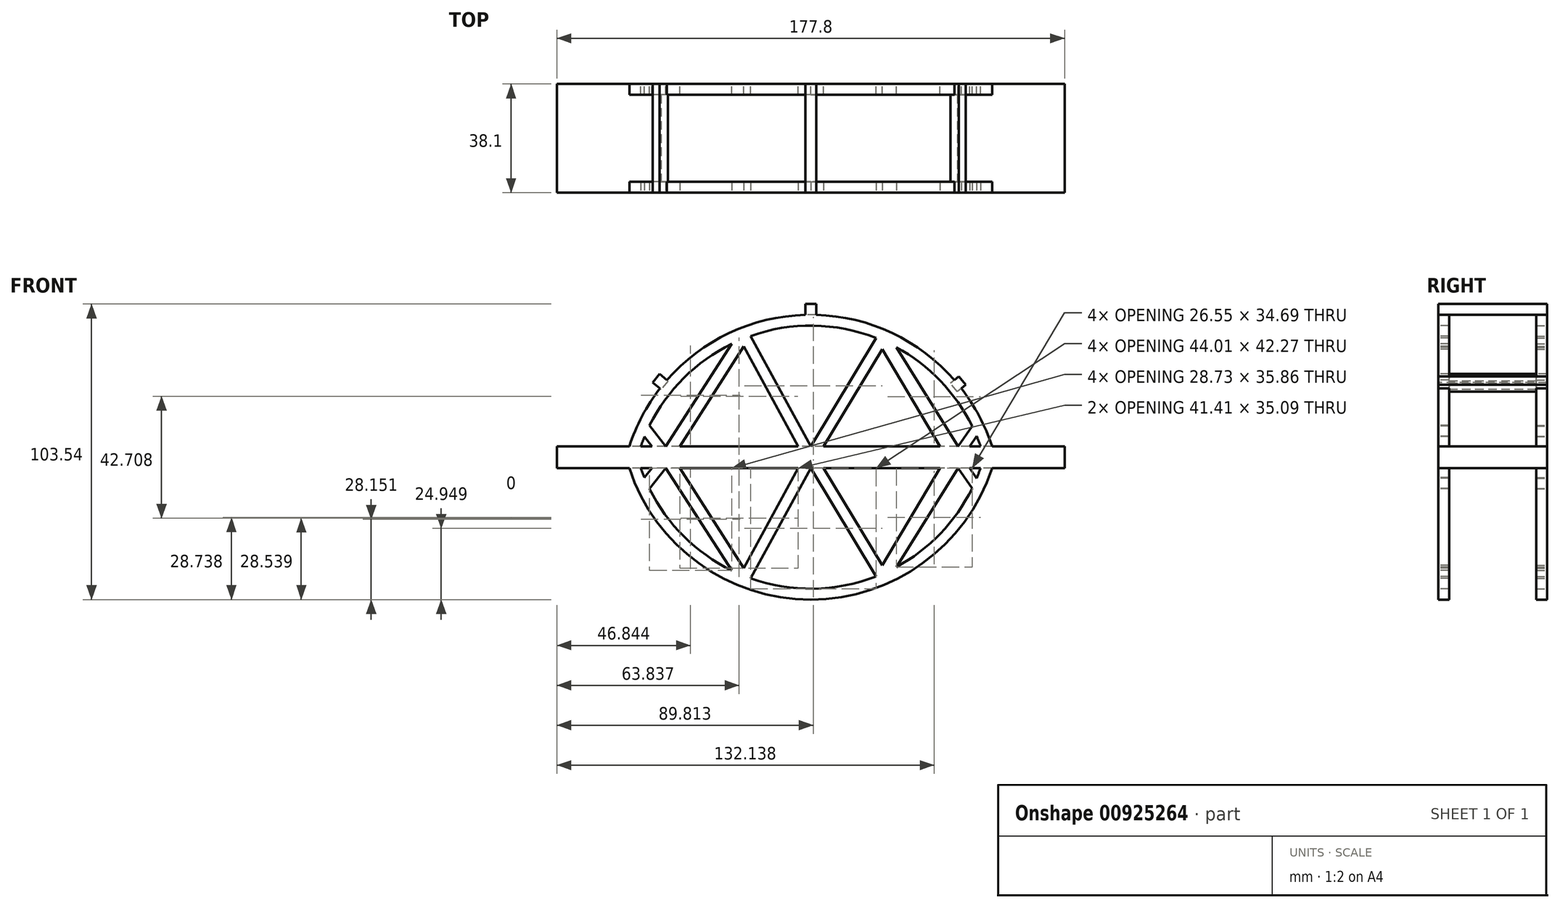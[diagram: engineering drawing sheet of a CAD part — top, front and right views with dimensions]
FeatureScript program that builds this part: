
annotation { "Feature Type Name" : "Feature", "Feature Type Description" : "" }
export const myFeature = defineFeature(function(context is Context, id is Id, definition is map)
    precondition{}
    {
        {
            var Q0;
            Q0=qCreatedBy(makeId("Front.planeOp"),FACE);
            var sketch = newSketch(context, id + "F0", { "sketchPlane" : qUnion([Q0])});
            skLineSegment(sketch, "E0.top", {"start": v(-44.28, -25.57) * mm, "end": v(-11.66, -25.57) * mm});
            skLineSegment(sketch, "E0.left", {"start": v(-47, -21.76) * mm, "end": v(-47, -25.57) * mm});
            skLineSegment(sketch, "E0.right", {"start": v(80, -21.76) * mm, "end": v(80, -25.57) * mm});
            skLineSegment(sketch, "E1", {"start": v(75.99, -21.76) * mm, "end": v(72.12, -21.76) * mm});
            skArc(sketch, "E2", {"start": v(80, -21.76) * mm, "mid": v(16.5, 24.33) * mm, "end": v(-47, -21.76) * mm});
            skLineSegment(sketch, "E3", {"start": v(16.5, -21.76) * mm, "end": v(-4.58, 16.88) * mm});
            skLineSegment(sketch, "E4", {"start": v(-11.18, 14.1) * mm, "end": v(-34.3, -21.76) * mm});
            skLineSegment(sketch, "E5", {"start": v(-34.3, -21.76) * mm, "end": v(-39.91, -14.48) * mm});
            skLineSegment(sketch, "E6", {"start": v(16.5, -21.76) * mm, "end": v(39.43, 16.2) * mm});
            skLineSegment(sketch, "E7", {"start": v(46.47, 12.93) * mm, "end": v(68.06, -21.76) * mm});
            skLineSegment(sketch, "E8", {"start": v(68.06, -21.76) * mm, "end": v(73.03, -14.67) * mm});
            skLineSegment(sketch, "E9.0", {"start": v(12.15, -21.76) * mm, "end": v(-7, 13.33) * mm});
            skLineSegment(sketch, "E10.0", {"start": v(21, -21.76) * mm, "end": v(41.54, 12.26) * mm});
            skLineSegment(sketch, "E11.0", {"start": v(72.12, -21.76) * mm, "end": v(74.62, -18.19) * mm});
            skLineSegment(sketch, "E12.trimOffspring", {"start": v(-39.1, -21.76) * mm, "end": v(-41.7, -18.4) * mm});
            skLineSegment(sketch, "E13.trimOffspring", {"start": v(-7, 13.33) * mm, "end": v(-29.26, -21.76) * mm});
            skLineSegment(sketch, "E14.trimOffspring", {"start": v(12.15, -21.76) * mm, "end": v(-29.26, -21.76) * mm});
            skLineSegment(sketch, "E15.trimOffspring", {"start": v(-39.1, -21.76) * mm, "end": v(-42.97, -21.76) * mm});
            skLineSegment(sketch, "E16.trimOffspring", {"start": v(41.54, 12.26) * mm, "end": v(61.77, -21.76) * mm});
            skLineSegment(sketch, "E17.trimOffspring", {"start": v(61.77, -21.76) * mm, "end": v(21, -21.76) * mm});
            skArc(sketch, "E18.0", {"start": v(75.99, -21.76) * mm, "mid": v(75.33, -19.96) * mm, "end": v(74.62, -18.19) * mm});
            skPoint(sketch, "E19.trimOffspring.end.orphan", {"position": v(-8.9, -21.76) * mm});
            skPoint(sketch, "E20.orphan", {"position": v(-42.49, -11.14) * mm});
            skArc(sketch, "E21.trimOffspring", {"start": v(-41.7, -18.4) * mm, "mid": v(-42.36, -20.07) * mm, "end": v(-42.97, -21.76) * mm});
            skArc(sketch, "E22.trimOffspring", {"start": v(-11.18, 14.1) * mm, "mid": v(-27.9, 2.19) * mm, "end": v(-39.91, -14.48) * mm});
            skArc(sketch, "E23.trimOffspring", {"start": v(39.43, 16.2) * mm, "mid": v(17.49, 20.5) * mm, "end": v(-4.58, 16.88) * mm});
            skArc(sketch, "E24.trimOffspring", {"start": v(39.12, 16.32) * mm, "mid": v(17.2, 20.51) * mm, "end": v(-4.8, 16.8) * mm});
            skPoint(sketch, "E25.orphan", {"position": v(75.5, -11.14) * mm});
            skArc(sketch, "E26.trimOffspring", {"start": v(73.03, -14.67) * mm, "mid": v(61.9, 1.2) * mm, "end": v(46.47, 12.93) * mm});
            skArc(sketch, "E27.trimOffspring", {"start": v(39.43, 16.2) * mm, "mid": v(17.37, 20.51) * mm, "end": v(-4.8, 16.8) * mm});
            skPoint(sketch, "E28.trimOffspring.end.orphan", {"position": v(41.9, -21.76) * mm});
            skPoint(sketch, "E29.start.orphan", {"position": v(16.5, 50.63) * mm});
            skPoint(sketch, "E30.orphan", {"position": v(-47, 50.63) * mm});
            skPoint(sketch, "E31.orphan", {"position": v(80, 50.63) * mm});
            skLineSegment(sketch, "E32", {"start": v(80, -21.76) * mm, "end": v(-47, -21.76) * mm});
            skPoint(sketch, "E33", {"position": v(16.5, 24.33) * mm});
            skPoint(sketch, "E34", {"position": v(68.06, 0) * mm});
            skPoint(sketch, "E35.positionSnap0", {"position": v(61.9, 1.2) * mm});
            skLineSegment(sketch, "E36.trimOffspring", {"start": v(-6.01, -25.57) * mm, "end": v(12.98, -25.57) * mm});
            skLineSegment(sketch, "E37.trimOffspring", {"start": v(19.96, -25.57) * mm, "end": v(39.03, -25.57) * mm});
            skLineSegment(sketch, "E38.trimOffspring", {"start": v(44.66, -25.57) * mm, "end": v(77.29, -25.57) * mm});
            skLineSegment(sketch, "E39", {"start": v(80, -25.57) * mm, "end": v(-47, -25.57) * mm});
            skLineSegment(sketch, "E40", {"start": v(41.69, -25.98) * mm, "end": v(42.08, -25.98) * mm});
            skPoint(sketch, "E41.orphan", {"position": v(41.9, -25.57) * mm});
            skLineSegment(sketch, "E42", {"start": v(16.03, -26.06) * mm, "end": v(16.96, -26.06) * mm});
            skPoint(sketch, "E43.orphan", {"position": v(16.5, -25.57) * mm});
            skLineSegment(sketch, "E44", {"start": v(-9.09, -26.03) * mm, "end": v(-8.52, -26.27) * mm});
            skPoint(sketch, "E45.orphan", {"position": v(-8.9, -25.57) * mm});
            skPoint(sketch, "E46", {"position": v(41.54, 19.46) * mm});
            skPoint(sketch, "E47", {"position": v(-7.55, 19.85) * mm});
            skPoint(sketch, "E48", {"position": v(-35.05, 0) * mm});
            skSolve(sketch);
        }
        {
            var Q0;
            {var subQ7=sQuery(id+"F0.wireOp",EDGE,"E0.left");Q0=makeQuery(id+"F0.imprint","IMPRINT",FACE,{"disambiguationData":[TD([[makeQuery(id+"F0.imprint","IMPRINT",EDGE,{"derivedFrom":subQ7}),1.0]])]});}
            extrude(context, id + "F1", {"entities" : qUnion([Q0]), "depth" : 19.05 * mm, "offsetDistance" : 25.4 * mm});
        }
        {
            var Q0;
            {var subQ6=sQuery(id+"F0.wireOp",EDGE,"E2");Q0=makeQuery(id+"F0.imprint","IMPRINT",FACE,{"disambiguationData":[TD([[makeQuery(id+"F0.imprint","IMPRINT",EDGE,{"derivedFrom":subQ6}),1.0]])]});}
            var Q1;
            {var subQ9=sQuery(id+"F0.wireOp",EDGE,"E0.left");Q1=makeQuery(id+"F0.imprint","IMPRINT",FACE,{"disambiguationData":[TD([[makeQuery(id+"F0.imprint","IMPRINT",EDGE,{"derivedFrom":subQ9}),1.0]])]});}
            extrude(context, id + "F2", {"entities" : qUnion([Q0, Q1]), "operationType" : NewBodyOperationType.ADD, "depth" : 3.8 * mm, "offsetDistance" : 25.4 * mm});
        }
        {
            var Q0;
            Q0=makeQuery(id+"F1.opExtrude","SWEPT_BODY",BODY,{"disambiguationData":[OSD([sQuery(id+"F0.wireOp",EDGE,"E0.left"),sQuery(id+"F0.wireOp",EDGE,"E0.right"),sQuery(id+"F0.wireOp",EDGE,"E32"),sQuery(id+"F0.wireOp",EDGE,"E39")])]});
            var Q1;
            Q1=makeQuery(id+"F1.opExtrude","CAP_FACE",FACE,{"disambiguationData":[OSD([sQuery(id+"F0.wireOp",EDGE,"E0.left"),sQuery(id+"F0.wireOp",EDGE,"E0.right"),sQuery(id+"F0.wireOp",EDGE,"E32"),sQuery(id+"F0.wireOp",EDGE,"E39")])],"isStart":false});
            mirror(context, id + "F3", {"operationType" : NewBodyOperationType.ADD, "entities" : qUnion([Q0]), "mirrorPlane" : qUnion([Q1])});
        }
        {
            var Q0;
            Q0=makeQuery(id+"F1.opExtrude","SWEPT_BODY",BODY,{"disambiguationData":[OSD([sQuery(id+"F0.wireOp",EDGE,"E0.left"),sQuery(id+"F0.wireOp",EDGE,"E0.right"),sQuery(id+"F0.wireOp",EDGE,"E32"),sQuery(id+"F0.wireOp",EDGE,"E39")])]});
            var Q1;
            {var subQ0=makeQuery(id+"F1.opExtrude","SWEPT_FACE",FACE,{"disambiguationData":[OSD([sQuery(id+"F0.wireOp",EDGE,"E39")])]});Q1=makeQuery(id+"F3.boolean.opBoolean","MERGE",FACE,{"derivedFrom":[subQ0,makeQuery(id+"F3.opPattern","COPY",FACE,{"derivedFrom":subQ0,"instanceName":"1"})]});}
            mirror(context, id + "F4", {"operationType" : NewBodyOperationType.ADD, "entities" : qUnion([Q0]), "mirrorPlane" : qUnion([Q1])});
        }
        {
            var Q0;
            {var subQ0=makeQuery(id+"F1.opExtrude","SWEPT_FACE",FACE,{"disambiguationData":[OSD([sQuery(id+"F0.wireOp",EDGE,"E0.right")])]});var subQ1=makeQuery(id+"F3.boolean.opBoolean","MERGE",FACE,{"derivedFrom":[subQ0,makeQuery(id+"F3.opPattern","COPY",FACE,{"derivedFrom":subQ0,"instanceName":"1"})]});Q0=makeQuery(id+"F4.boolean.opBoolean","MERGE",FACE,{"derivedFrom":[subQ1,makeQuery(id+"F4.opPattern","COPY",FACE,{"derivedFrom":subQ1,"instanceName":"1"})]});}
            var sketch = newSketch(context, id + "F5", { "sketchPlane" : qUnion([Q0])});
            skLineSegment(sketch, "E49.bottom", {"start": v(-38.1, -21.76) * mm, "end": v(0, -21.76) * mm});
            skLineSegment(sketch, "E49.top", {"start": v(-38.1, -29.38) * mm, "end": v(0, -29.38) * mm});
            skLineSegment(sketch, "E49.left", {"start": v(-38.1, -21.76) * mm, "end": v(-38.1, -29.38) * mm});
            skLineSegment(sketch, "E49.right", {"start": v(0, -21.76) * mm, "end": v(0, -29.38) * mm});
            skSolve(sketch);
        }
        {
            var Q0;
            {var subQ3=sQuery(id+"F5.wireOp",EDGE,"E49.left");Q0=makeQuery(id+"F5.imprint","IMPRINT",FACE,{"disambiguationData":[TD([[makeQuery(id+"F5.imprint","IMPRINT",EDGE,{"derivedFrom":subQ3}),1.0]])]});}
            extrude(context, id + "F6", {"entities" : qUnion([Q0]), "operationType" : NewBodyOperationType.ADD, "depth" : 25.4 * mm, "offsetDistance" : 25.4 * mm});
        }
        {
            var Q0;
            {var subQ0=makeQuery(id+"F1.opExtrude","SWEPT_FACE",FACE,{"disambiguationData":[OSD([sQuery(id+"F0.wireOp",EDGE,"E0.left")])]});var subQ1=makeQuery(id+"F3.boolean.opBoolean","MERGE",FACE,{"derivedFrom":[subQ0,makeQuery(id+"F3.opPattern","COPY",FACE,{"derivedFrom":subQ0,"instanceName":"1"})]});Q0=makeQuery(id+"F4.boolean.opBoolean","MERGE",FACE,{"derivedFrom":[subQ1,makeQuery(id+"F4.opPattern","COPY",FACE,{"derivedFrom":subQ1,"instanceName":"1"})]});}
            var sketch = newSketch(context, id + "F7", { "sketchPlane" : qUnion([Q0])});
            skLineSegment(sketch, "E50.bottom", {"start": v(0, -21.76) * mm, "end": v(38.1, -21.76) * mm});
            skLineSegment(sketch, "E50.top", {"start": v(0, -29.38) * mm, "end": v(38.1, -29.38) * mm});
            skLineSegment(sketch, "E50.left", {"start": v(0, -21.76) * mm, "end": v(0, -29.38) * mm});
            skLineSegment(sketch, "E50.right", {"start": v(38.1, -21.76) * mm, "end": v(38.1, -29.38) * mm});
            skSolve(sketch);
        }
        {
            var Q0;
            {var subQ6=sQuery(id+"F7.wireOp",EDGE,"E50.left");Q0=makeQuery(id+"F7.imprint","IMPRINT",FACE,{"disambiguationData":[TD([[makeQuery(id+"F7.imprint","IMPRINT",EDGE,{"derivedFrom":subQ6}),1.0]])]});}
            extrude(context, id + "F8", {"entities" : qUnion([Q0]), "operationType" : NewBodyOperationType.ADD, "depth" : 25.4 * mm, "offsetDistance" : 25.4 * mm});
        }
        {
            var Q0;
            Q0=sQuery(id+"F0.wireOp",VERTEX,"E34");
            var Q1;
            Q1=sQuery(id+"F0.wireOp",EDGE,"E2");
            cPlane(context, id + "F9", {"entities" : qUnion([Q0, Q1]), "cplaneType" : CPlaneType.CURVE_POINT, "offset" : 25.4 * mm, "width" : 152.4 * mm, "height" : 152.4 * mm});
        }
        {
            var Q0;
            Q0=qCreatedBy(id+"F9.planeOp",FACE);
            var sketch = newSketch(context, id + "F10", { "sketchPlane" : qUnion([Q0])});
            skLineSegment(sketch, "E51.bottom", {"start": v(50.72, 0) * mm, "end": v(54.53, 0) * mm});
            skLineSegment(sketch, "E51.top", {"start": v(50.72, -38.1) * mm, "end": v(54.53, -38.1) * mm});
            skLineSegment(sketch, "E51.left", {"start": v(50.72, 0) * mm, "end": v(50.72, -38.1) * mm});
            skLineSegment(sketch, "E51.right", {"start": v(54.53, 0) * mm, "end": v(54.53, -38.1) * mm});
            skLineSegment(sketch, "E52.1.0", {"start": v(-25.36, 43.92) * mm, "end": v(-27.26, 47.22) * mm});
            skLineSegment(sketch, "E52.2.0", {"start": v(-25.36, -43.92) * mm, "end": v(-27.26, -47.22) * mm});
            skPoint(sketch, "E52.center", {"position": v(0, 0) * mm});
            skSolve(sketch);
        }
        {
            var Q0;
            Q0=makeQuery(id+"F10.imprint","IMPRINT",FACE,{"disambiguationData":[TD([[makeQuery(id+"F10.imprint","IMPRINT",EDGE,{"derivedFrom":sQuery(id+"F10.wireOp",EDGE,"E51.bottom")}),-1.0]])]});
            extrude(context, id + "F11", {"entities" : qUnion([Q0]), "operationType" : NewBodyOperationType.ADD, "endBound" : BoundingType.SYMMETRIC, "depth" : 3.8 * mm, "offsetDistance" : 25.4 * mm});
        }
        {
            var Q0;
            Q0=sQuery(id+"F0.wireOp",VERTEX,"E33");
            var Q1;
            Q1=sQuery(id+"F0.wireOp",EDGE,"E2");
            cPlane(context, id + "F12", {"entities" : qUnion([Q0, Q1]), "cplaneType" : CPlaneType.CURVE_POINT, "offset" : 25.4 * mm, "width" : 152.4 * mm, "height" : 152.4 * mm});
        }
        {
            var Q0;
            Q0=qCreatedBy(id+"F12.planeOp",FACE);
            var sketch = newSketch(context, id + "F13", { "sketchPlane" : qUnion([Q0])});
            skLineSegment(sketch, "E53.bottom", {"start": v(0, 24.27) * mm, "end": v(38.1, 24.27) * mm});
            skLineSegment(sketch, "E53.top", {"start": v(0, 28.08) * mm, "end": v(38.1, 28.08) * mm});
            skLineSegment(sketch, "E53.left", {"start": v(0, 24.27) * mm, "end": v(0, 28.08) * mm});
            skLineSegment(sketch, "E53.right", {"start": v(38.1, 24.27) * mm, "end": v(38.1, 28.08) * mm});
            skSolve(sketch);
        }
        {
            var Q0;
            Q0=makeQuery(id+"F13.imprint","IMPRINT",FACE,{"disambiguationData":[TD([[makeQuery(id+"F13.imprint","IMPRINT",EDGE,{"derivedFrom":sQuery(id+"F13.wireOp",EDGE,"E53.bottom")}),1.0]])]});
            extrude(context, id + "F14", {"entities" : qUnion([Q0]), "operationType" : NewBodyOperationType.ADD, "endBound" : BoundingType.SYMMETRIC, "depth" : 3.8 * mm, "offsetDistance" : 25.4 * mm});
        }
        {
            var Q0;
            Q0=sQuery(id+"F0.wireOp",VERTEX,"E48");
            var Q1;
            Q1=sQuery(id+"F0.wireOp",EDGE,"E2");
            cPlane(context, id + "F15", {"entities" : qUnion([Q0, Q1]), "cplaneType" : CPlaneType.CURVE_POINT, "offset" : 25.4 * mm, "width" : 152.4 * mm, "height" : 152.4 * mm});
        }
        {
            var Q0;
            Q0=qCreatedBy(id+"F15.planeOp",FACE);
            var sketch = newSketch(context, id + "F16", { "sketchPlane" : qUnion([Q0])});
            skLineSegment(sketch, "E54.bottom", {"start": v(-26.53, 0) * mm, "end": v(-30.34, 0) * mm});
            skLineSegment(sketch, "E54.top", {"start": v(-26.53, 38.1) * mm, "end": v(-30.34, 38.1) * mm});
            skLineSegment(sketch, "E54.left", {"start": v(-26.53, 0) * mm, "end": v(-26.53, 38.1) * mm});
            skLineSegment(sketch, "E54.right", {"start": v(-30.34, 0) * mm, "end": v(-30.34, 38.1) * mm});
            skSolve(sketch);
        }
        {
            var Q0;
            Q0=makeQuery(id+"F16.imprint","IMPRINT",FACE,{"disambiguationData":[TD([[makeQuery(id+"F16.imprint","IMPRINT",EDGE,{"derivedFrom":sQuery(id+"F16.wireOp",EDGE,"E54.bottom")}),-1.0]])]});
            extrude(context, id + "F17", {"entities" : qUnion([Q0]), "operationType" : NewBodyOperationType.ADD, "endBound" : BoundingType.SYMMETRIC, "depth" : 3.8 * mm, "offsetDistance" : 25.4 * mm});
        }
        {
            var Q0;
            {var subQ0=sQuery(id+"F0.wireOp",EDGE,"E39");var subQ1=sQuery(id+"F0.wireOp",EDGE,"E32");var subQ2=sQuery(id+"F0.wireOp",EDGE,"E0.right");var subQ3=sQuery(id+"F0.wireOp",EDGE,"E0.left");var subQ4=makeQuery(id+"F3.opPattern","COPY",FACE,{"derivedFrom":makeQuery(id+"F2.boolean.opBoolean","MERGE",FACE,{"derivedFrom":[makeQuery(id+"F1.opExtrude","CAP_FACE",FACE,{"disambiguationData":[OSD([subQ3,subQ2,subQ1,subQ0])],"isStart":true}),makeQuery(id+"F2.opExtrude","CAP_FACE",FACE,{"disambiguationData":[OSD([subQ3,subQ2,sQuery(id+"F0.wireOp",EDGE,"E2"),sQuery(id+"F0.wireOp",EDGE,"E3"),sQuery(id+"F0.wireOp",EDGE,"E4"),sQuery(id+"F0.wireOp",EDGE,"E5"),sQuery(id+"F0.wireOp",EDGE,"E6"),sQuery(id+"F0.wireOp",EDGE,"E7"),sQuery(id+"F0.wireOp",EDGE,"E8"),sQuery(id+"F0.wireOp",EDGE,"E9.0"),sQuery(id+"F0.wireOp",EDGE,"E10.0"),sQuery(id+"F0.wireOp",EDGE,"E11.0"),sQuery(id+"F0.wireOp",EDGE,"E12.trimOffspring"),sQuery(id+"F0.wireOp",EDGE,"E13.trimOffspring"),sQuery(id+"F0.wireOp",EDGE,"E16.trimOffspring"),sQuery(id+"F0.wireOp",EDGE,"E18.0"),sQuery(id+"F0.wireOp",EDGE,"E22.trimOffspring"),sQuery(id+"F0.wireOp",EDGE,"E27.trimOffspring"),sQuery(id+"F0.wireOp",EDGE,"E21.trimOffspring"),sQuery(id+"F0.wireOp",EDGE,"E26.trimOffspring"),subQ1,subQ0])],"isStart":true})]}),"instanceName":"1"});Q0=makeQuery(id+"F17.boolean.opBoolean","MERGE",FACE,{"derivedFrom":[makeQuery(id+"F14.boolean.opBoolean","MERGE",FACE,{"derivedFrom":[makeQuery(id+"F11.boolean.opBoolean","MERGE",FACE,{"derivedFrom":[makeQuery(id+"F8.boolean.opBoolean","MERGE",FACE,{"derivedFrom":[makeQuery(id+"F6.boolean.opBoolean","MERGE",FACE,{"derivedFrom":[makeQuery(id+"F4.boolean.opBoolean","MERGE",FACE,{"derivedFrom":[subQ4,makeQuery(id+"F4.opPattern","COPY",FACE,{"derivedFrom":subQ4,"instanceName":"1"})]}),makeQuery(id+"F6.opExtrude","SWEPT_FACE",FACE,{"disambiguationData":[OSD([sQuery(id+"F5.wireOp",EDGE,"E49.left")])]})]}),makeQuery(id+"F8.opExtrude","SWEPT_FACE",FACE,{"disambiguationData":[OSD([sQuery(id+"F7.wireOp",EDGE,"E50.right")])]})]}),makeQuery(id+"F11.opExtrude","SWEPT_FACE",FACE,{"disambiguationData":[OSD([sQuery(id+"F10.wireOp",EDGE,"E51.top")])]})]}),makeQuery(id+"F14.opExtrude","SWEPT_FACE",FACE,{"disambiguationData":[OSD([sQuery(id+"F13.wireOp",EDGE,"E53.right")])]})]}),makeQuery(id+"F17.opExtrude","SWEPT_FACE",FACE,{"disambiguationData":[OSD([sQuery(id+"F16.wireOp",EDGE,"E54.top")])]})]});}
            var sketch = newSketch(context, id + "F18", { "sketchPlane" : qUnion([Q0])});
            skPoint(sketch, "E55", {"position": v(47.37, -67.89) * mm});
            skPoint(sketch, "E56", {"position": v(16.51, -75.4) * mm});
            skPoint(sketch, "E57", {"position": v(-28.3, -58.2) * mm});
            skSolve(sketch);
        }
    });
